# Revit family: F1S_2863-2862-2606_OS265
name_source: partatom
category: Finestre
units: mm (PartAtom-declared; Revit-internal decimal feet)

## family parameters
Condiviso = No
Host = Muro
Numero OmniClass = 23.30.20.00
Punto di calcolo locali = Sì
Sempre verticale = Sì
Taglio con vuoti quando caricato = No
Titolo OmniClass = Windows

## types (4) — shared parameters
Altezza di default del davanzale = 800 mm  [stored 2.62467 ft]
Chiusura muro = Per host
Costruzione analitica = <Nessuno>
Descrizione = Finestra apertura a sporgere
H_Max = 1800 mm
H_Min = 800 mm  [stored 2.62467 ft]
L = 900 mm  [stored 2.95276 ft]
L1 = 900 mm  [stored 2.95276 ft]
L_Max = 900 mm  [stored 2.95276 ft]
L_Min = 400 mm  [stored 1.31234 ft]
L_vetro = 824 mm  [stored 2.70341 ft]
Modello = OS2 65
Nota tecnica = https://s3-eu-central-1.amazonaws.com
Produttore = Secco Sistemi Spa
URL = https://www.seccosistemi.com
WARNING = Sì

## per-type parameters (varying)
| type | Altezza | H | H1 | H_vetro | Larghezza | MATERIALE |
| Acciaio zincato | 1500 mm  [stored 4.92126 ft] | 1500 mm  [stored 4.92126 ft] | 1500 mm  [stored 4.92126 ft] | 1424 mm  [stored 4.67192 ft] | 1500 mm  [stored 4.92126 ft] | Acciaio |
| Acciaio inox | 1500 mm  [stored 4.92126 ft] | 1500 mm  [stored 4.92126 ft] | 1500 mm  [stored 4.92126 ft] | 1424 mm  [stored 4.67192 ft] | 1500 mm  [stored 4.92126 ft] | Acciaio inox, spazzolato |
| Acciaio corten | 1500 mm  [stored 4.92126 ft] | 1500 mm  [stored 4.92126 ft] | 1500 mm  [stored 4.92126 ft] | 1424 mm  [stored 4.67192 ft] | 1500 mm  [stored 4.92126 ft] | Acciaio corten |
| Ottone | 500 mm  [stored 1.64042 ft] | 800 mm  [stored 2.62467 ft] | 800 mm  [stored 2.62467 ft] | 724 mm  [stored 2.37533 ft] | 1000 mm  [stored 3.28084 ft] | Ottone |

note: [stored X ft] marks values corroborated as IEEE doubles in the binary element streams (Revit-internal decimal feet)
